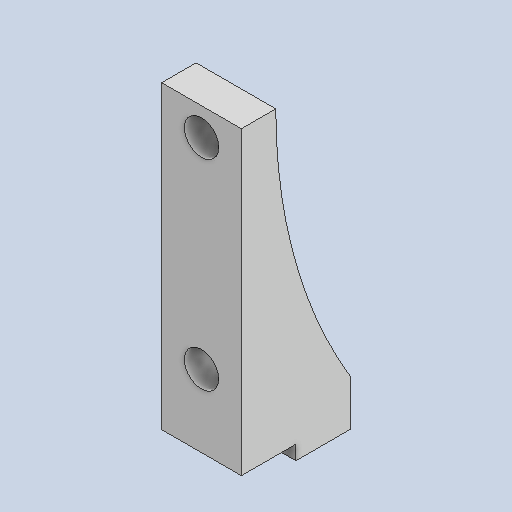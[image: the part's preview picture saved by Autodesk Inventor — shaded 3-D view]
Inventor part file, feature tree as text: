
AUTODESK INVENTOR PART (.ipt)
format: ipt  version: 2022 (Build 260153070, 153G)  size: 126,976 bytes
history: native  units: in
note: dims shown in document units (in); Inventor stores cm internally (conversion verified against a paired STEP export)
features: sketch x4, other x3
ambient origin geometry x8: Origin, YZ Plane, XZ Plane, XY Plane, X Axis, Y Axis, Z Axis, Center Point
bodies: Solid1 (feature_tree)
feature tree (7):
  other  "ENCODERV2PLATE.ipt"
  other  "Solid1::ENCODERV2PLATE.ipt"
  other  "TaggingFeature1"
  sketch  "Sketch1"  dims[d0=0.3937in]
  sketch  "Sketch2"
  sketch  "Sketch3"
  sketch  "Sketch4"
